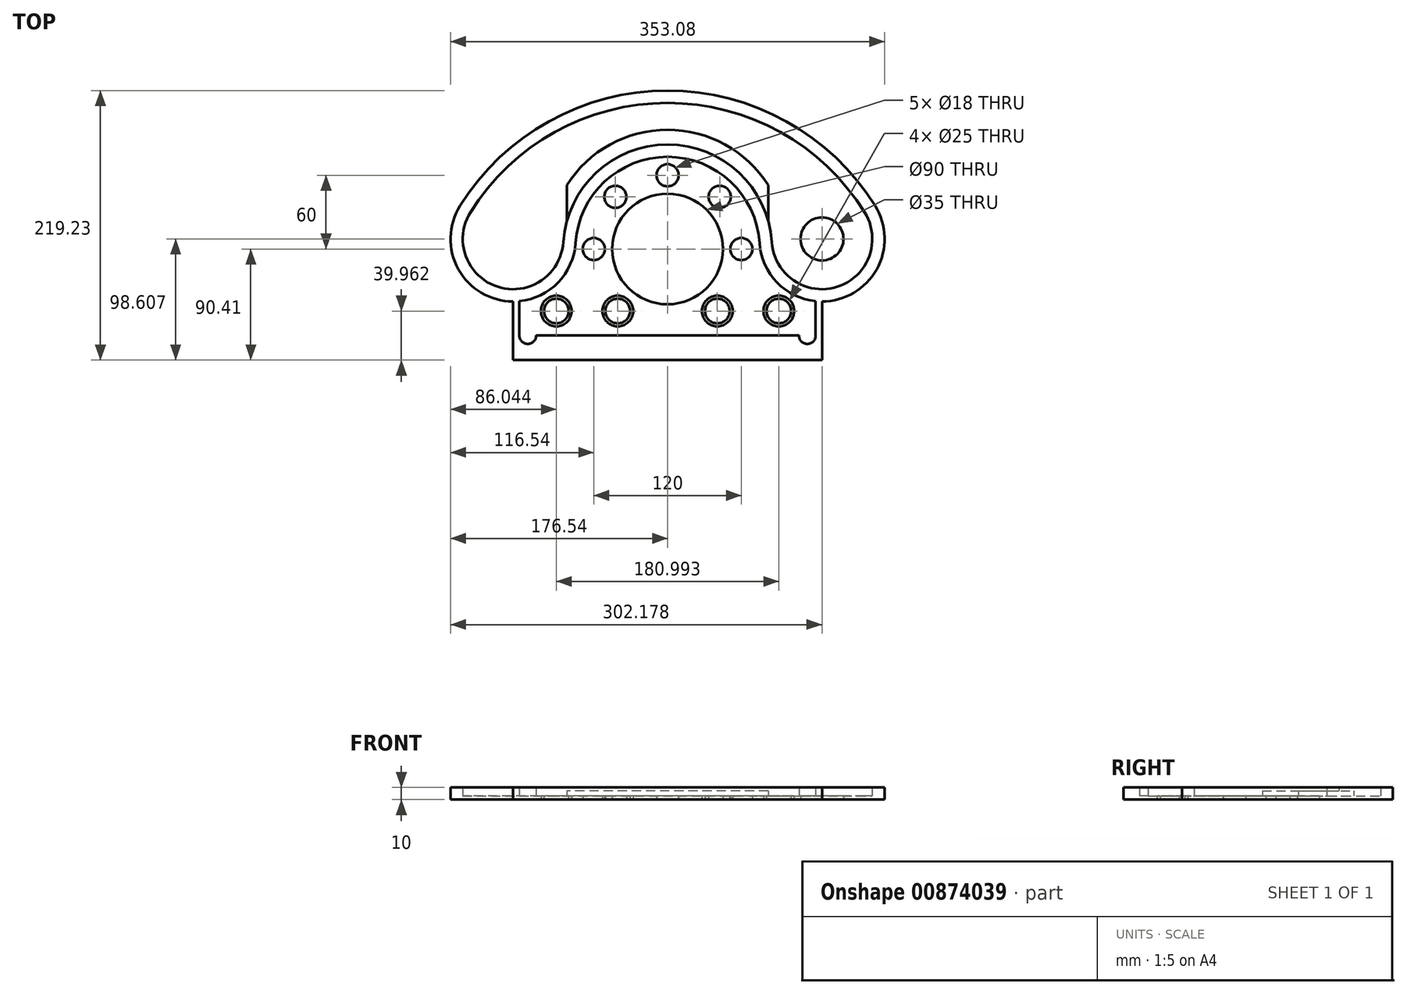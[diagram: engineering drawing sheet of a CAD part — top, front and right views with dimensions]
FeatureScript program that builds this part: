
annotation { "Feature Type Name" : "Feature", "Feature Type Description" : "" }
export const myFeature = defineFeature(function(context is Context, id is Id, definition is map)
    precondition{}
    {
        {
            var Q0;
            Q0=qCreatedBy(makeId("Top.planeOp"),FACE);
            var sketch = newSketch(context, id + "F0", { "sketchPlane" : qUnion([Q0])});
            skCircle(sketch, "E0", {"center": v(0, 0) * mm, "radius": 45 * mm});
            skArc(sketch, "E1", {"start": v(74.84, 4.88) * mm, "mid": v(0, 75) * mm, "end": v(-74.84, 4.88) * mm});
            skArc(sketch, "E2", {"start": v(84.82, 5.53) * mm, "mid": v(0, 85) * mm, "end": v(-84.82, 5.53) * mm});
            skLineSegment(sketch, "E3", {"start": v(-125.64, -32.7) * mm, "end": v(-125.64, -90.4) * mm});
            skLineSegment(sketch, "E4", {"start": v(-125.64, -90.4) * mm, "end": v(0, -90.4) * mm});
            skArc(sketch, "E5", {"start": v(-125.64, -32.7) * mm, "mid": v(-97.67, -21.65) * mm, "end": v(-84.82, 5.53) * mm});
            skArc(sketch, "E6", {"start": v(-120.5, -42.45) * mm, "mid": v(-89, -27.14) * mm, "end": v(-74.84, 4.88) * mm});
            skLineSegment(sketch, "E7", {"start": v(-120.5, -42.45) * mm, "end": v(-120.5, -70.4) * mm});
            skArc(sketch, "E8", {"start": v(-120.5, -70.4) * mm, "mid": v(-113.7, -77.21) * mm, "end": v(-106.9, -70.4) * mm});
            skLineSegment(sketch, "E9", {"start": v(-106.9, -70.4) * mm, "end": v(0, -70.4) * mm});
            skArc(sketch, "E10.MirrorCS", {"start": v(125.64, -32.7) * mm, "mid": v(97.67, -21.65) * mm, "end": v(84.82, 5.53) * mm});
            skArc(sketch, "E11.MirrorCS", {"start": v(120.5, -42.45) * mm, "mid": v(89, -27.14) * mm, "end": v(74.84, 4.88) * mm});
            skLineSegment(sketch, "E12.MirrorCS", {"start": v(125.64, -32.7) * mm, "end": v(125.64, -90.4) * mm});
            skLineSegment(sketch, "E13.MirrorCS", {"start": v(120.5, -42.45) * mm, "end": v(120.5, -70.4) * mm});
            skArc(sketch, "E14.MirrorCS", {"start": v(120.5, -70.4) * mm, "mid": v(113.7, -77.21) * mm, "end": v(106.9, -70.4) * mm});
            skLineSegment(sketch, "E15.MirrorCS", {"start": v(106.9, -70.4) * mm, "end": v(0, -70.4) * mm});
            skLineSegment(sketch, "E16.MirrorCS", {"start": v(125.64, -90.4) * mm, "end": v(0, -90.4) * mm});
            skPoint(sketch, "E17.orphan", {"position": v(125.64, -42.7) * mm});
            skPoint(sketch, "E18.orphan", {"position": v(-125.64, -42.7) * mm});
            skSolve(sketch);
        }
        {
            var Q0;
            {var subQ2=sQuery(id+"F0.wireOp",EDGE,"E1");Q0=makeQuery(id+"F0.imprint","IMPRINT",FACE,{"disambiguationData":[TD([[makeQuery(id+"F0.imprint","IMPRINT",EDGE,{"derivedFrom":subQ2}),-1.0]])]});}
            var Q1;
            Q1=makeQuery(id+"F0.imprint","IMPRINT",FACE,{"disambiguationData":[TD([[makeQuery(id+"F0.imprint","IMPRINT",EDGE,{"derivedFrom":sQuery(id+"F0.wireOp",EDGE,"E0")}),-1.0]])]});
            extrude(context, id + "F1", {"entities" : qUnion([Q0, Q1]), "depth" : 3 * mm, "offsetDistance" : 25 * mm});
        }
        {
            var Q0;
            Q0=qCreatedBy(makeId("Top.planeOp"),FACE);
            var sketch = newSketch(context, id + "F2", { "sketchPlane" : qUnion([Q0])});
            skPoint(sketch, "E19.0", {"position": v(125.64, 8.2) * mm});
            skPoint(sketch, "E20.0", {"position": v(125.64, -32.7) * mm});
            skArc(sketch, "E21", {"start": v(125.64, -32.7) * mm, "mid": v(161.4, -11.65) * mm, "end": v(160.35, 29.84) * mm});
            skArc(sketch, "E22", {"start": v(160.35, 29.84) * mm, "mid": v(91.69, 95.08) * mm, "end": v(0, 118.82) * mm});
            skArc(sketch, "E23.MirrorCS", {"start": v(-160.35, 29.84) * mm, "mid": v(-91.69, 95.08) * mm, "end": v(0, 118.82) * mm});
            skArc(sketch, "E24.MirrorC", {"start": v(-125.64, -32.7) * mm, "mid": v(-161.4, -11.65) * mm, "end": v(-160.35, 29.84) * mm});
            skArc(sketch, "E25.0", {"start": v(-125.64, -32.7) * mm, "mid": v(-97.67, -21.65) * mm, "end": v(-84.82, 5.53) * mm});
            skPoint(sketch, "E26.0", {"position": v(-81.93, 37.27) * mm});
            skArc(sketch, "E27.0", {"start": v(81.93, 51.92) * mm, "mid": v(0, 97) * mm, "end": v(-81.93, 51.92) * mm});
            skPoint(sketch, "E28.0", {"position": v(81.93, 37.27) * mm});
            skPoint(sketch, "E29.0", {"position": v(97.67, -21.65) * mm});
            skPoint(sketch, "E30.0", {"position": v(84.82, 5.53) * mm});
            skArc(sketch, "E31.0", {"start": v(125.64, -32.7) * mm, "mid": v(97.67, -21.65) * mm, "end": v(84.82, 5.53) * mm});
            skPoint(sketch, "E32.0", {"position": v(81.93, 22.63) * mm});
            skPoint(sketch, "E33.0", {"position": v(0, 85) * mm});
            skArc(sketch, "E34.0", {"start": v(84.82, 5.53) * mm, "mid": v(83.81, 14.15) * mm, "end": v(81.93, 22.63) * mm});
            skLineSegment(sketch, "E35.0", {"start": v(81.93, 22.63) * mm, "end": v(81.93, 51.92) * mm});
            skLineSegment(sketch, "E36.0", {"start": v(-81.93, 22.63) * mm, "end": v(-81.93, 51.92) * mm});
            skPoint(sketch, "E37.0", {"position": v(-81.93, 22.63) * mm});
            skPoint(sketch, "E38.0.end.orphan", {"position": v(-84.82, 5.53) * mm});
            skArc(sketch, "E39.0", {"start": v(-81.93, 22.63) * mm, "mid": v(-83.81, 14.15) * mm, "end": v(-84.82, 5.53) * mm});
            skSolve(sketch);
        }
        {
            var Q0;
            {var subQ2=sQuery(id+"F0.wireOp",EDGE,"E1");Q0=makeQuery(id+"F0.imprint","IMPRINT",FACE,{"disambiguationData":[TD([[makeQuery(id+"F0.imprint","IMPRINT",EDGE,{"derivedFrom":subQ2}),-1.0]])]});}
            extrude(context, id + "F3", {"entities" : qUnion([Q0]), "operationType" : NewBodyOperationType.ADD, "depth" : 10 * mm, "offsetDistance" : 25 * mm});
        }
        {
            var Q0;
            Q0=qCreatedBy(makeId("Top.planeOp"),FACE);
            var sketch = newSketch(context, id + "F4", { "sketchPlane" : qUnion([Q0])});
            skArc(sketch, "E40", {"start": v(81.93, 51.92) * mm, "mid": v(0, 97) * mm, "end": v(-81.93, 51.92) * mm});
            skLineSegment(sketch, "E41", {"start": v(-81.93, 22.63) * mm, "end": v(-81.93, 51.92) * mm});
            skArc(sketch, "E42.0", {"start": v(84.82, 5.53) * mm, "mid": v(0, 85) * mm, "end": v(-84.82, 5.53) * mm});
            skLineSegment(sketch, "E43.MirrorCS", {"start": v(81.93, 22.63) * mm, "end": v(81.93, 51.92) * mm});
            skPoint(sketch, "E44.orphan", {"position": v(-81.93, 0) * mm});
            skPoint(sketch, "E45.orphan", {"position": v(81.93, 0) * mm});
            skSolve(sketch);
        }
        {
            var Q0;
            Q0=makeQuery(id+"F4.imprint","IMPRINT",FACE,{"disambiguationData":[TD([[makeQuery(id+"F4.imprint","IMPRINT",EDGE,{"derivedFrom":sQuery(id+"F4.wireOp",EDGE,"E40")}),1.0]])]});
            extrude(context, id + "F5", {"entities" : qUnion([Q0]), "operationType" : NewBodyOperationType.ADD, "depth" : 7 * mm, "offsetDistance" : 25 * mm});
        }
        {
            var Q0;
            Q0=qSketchRegion(id+"F2",true);
            extrude(context, id + "F6", {"entities" : qUnion([Q0]), "operationType" : NewBodyOperationType.ADD, "depth" : 3 * mm, "offsetDistance" : 25 * mm});
        }
        {
            var Q0;
            Q0=makeQuery(id+"F0.imprint","IMPRINT",FACE,{"disambiguationData":[TD([[makeQuery(id+"F0.imprint","IMPRINT",EDGE,{"derivedFrom":sQuery(id+"F0.wireOp",EDGE,"E0")}),1.0]])]});
            var sketch = newSketch(context, id + "F7", { "sketchPlane" : qUnion([Q0])});
            skPoint(sketch, "E46.0", {"position": v(125.64, -90.4) * mm});
            skPoint(sketch, "E47.0", {"position": v(120.5, -42.45) * mm});
            skPoint(sketch, "E48.0", {"position": v(125.64, 8.2) * mm});
            skPoint(sketch, "E49.0", {"position": v(-120.5, -42.45) * mm});
            skPoint(sketch, "E50.0", {"position": v(-125.64, 8.2) * mm});
            skPoint(sketch, "E51.0", {"position": v(-125.64, -90.4) * mm});
            skPoint(sketch, "E52.0", {"position": v(0, -70.15) * mm});
            skArc(sketch, "E53", {"start": v(125.64, -42.7) * mm, "mid": v(170.15, -16.5) * mm, "end": v(168.83, 35.13) * mm});
            skArc(sketch, "E54", {"start": v(-168.83, 35.13) * mm, "mid": v(-170.15, -16.5) * mm, "end": v(-125.64, -42.7) * mm});
            skArc(sketch, "E55", {"start": v(168.83, 35.13) * mm, "mid": v(0, 128.82) * mm, "end": v(-168.83, 35.13) * mm});
            skPoint(sketch, "E56.0", {"position": v(-125.64, -32.7) * mm});
            skPoint(sketch, "E57.0", {"position": v(-125.64, -42.7) * mm});
            skPoint(sketch, "E58.0", {"position": v(125.64, -32.7) * mm});
            skPoint(sketch, "E59.0", {"position": v(125.64, -42.7) * mm});
            skLineSegment(sketch, "E60", {"start": v(125.64, -42.7) * mm, "end": v(125.64, -32.7) * mm});
            skLineSegment(sketch, "E61", {"start": v(-125.64, -42.7) * mm, "end": v(-125.64, -32.7) * mm});
            skArc(sketch, "E62.2", {"start": v(125.64, -32.7) * mm, "mid": v(161.4, -11.65) * mm, "end": v(160.35, 29.84) * mm});
            skArc(sketch, "E62.3", {"start": v(160.35, 29.84) * mm, "mid": v(91.69, 95.08) * mm, "end": v(0, 118.82) * mm});
            skArc(sketch, "E62.4", {"start": v(-160.35, 29.84) * mm, "mid": v(-91.69, 95.08) * mm, "end": v(0, 118.82) * mm});
            skArc(sketch, "E62.5", {"start": v(-125.64, -32.7) * mm, "mid": v(-161.4, -11.65) * mm, "end": v(-160.35, 29.84) * mm});
            skPoint(sketch, "E62.9", {"position": v(-161.4, -11.65) * mm});
            skSolve(sketch);
        }
        {
            var Q0;
            Q0=makeQuery(id+"F7.imprint","IMPRINT",FACE,{"disambiguationData":[TD([[makeQuery(id+"F7.imprint","IMPRINT",EDGE,{"derivedFrom":sQuery(id+"F7.wireOp",EDGE,"E53")}),1.0]])]});
            extrude(context, id + "F8", {"entities" : qUnion([Q0]), "operationType" : NewBodyOperationType.ADD, "depth" : 10 * mm, "offsetDistance" : 25 * mm});
        }
        {
            var Q0;
            Q0=makeQuery(id+"F0.imprint","IMPRINT",FACE,{"disambiguationData":[TD([[makeQuery(id+"F0.imprint","IMPRINT",EDGE,{"derivedFrom":sQuery(id+"F0.wireOp",EDGE,"E0")}),1.0]])]});
            var sketch = newSketch(context, id + "F9", { "sketchPlane" : qUnion([Q0])});
            skPoint(sketch, "E63.0", {"position": v(125.64, 8.2) * mm});
            skPoint(sketch, "E64.0", {"position": v(-125.64, 8.2) * mm});
            skCircle(sketch, "E65", {"center": v(125.64, 8.2) * mm, "radius": 17.5 * mm});
            skPoint(sketch, "E66.0", {"position": v(120.5, -56.43) * mm});
            skPoint(sketch, "E67.0", {"position": v(-120.5, -56.43) * mm});
            skPoint(sketch, "E68.0", {"position": v(-120.5, -42.45) * mm});
            skPoint(sketch, "E69.0", {"position": v(120.5, -42.45) * mm});
            skLineSegment(sketch, "E70", {"start": v(-120.5, -42.45) * mm, "end": v(-120.5, -50.45) * mm});
            skLineSegment(sketch, "E71", {"start": v(-120.5, -50.45) * mm, "end": v(120.5, -50.45) * mm});
            skLineSegment(sketch, "E72", {"start": v(-120.5, -50.45) * mm, "end": v(-90.5, -50.45) * mm});
            skLineSegment(sketch, "E73", {"start": v(-90.5, -50.45) * mm, "end": v(9.5, -50.45) * mm});
            skLineSegment(sketch, "E74", {"start": v(-90.5, -50.45) * mm, "end": v(-40.5, -50.45) * mm});
            skLineSegment(sketch, "E75", {"start": v(120.5, -50.45) * mm, "end": v(90.5, -50.45) * mm});
            skLineSegment(sketch, "E76", {"start": v(90.5, -50.45) * mm, "end": v(40.5, -50.45) * mm});
            skCircle(sketch, "E77", {"center": v(-90.5, -50.45) * mm, "radius": 12.5 * mm});
            skCircle(sketch, "E78", {"center": v(-40.5, -50.45) * mm, "radius": 12.5 * mm});
            skCircle(sketch, "E79", {"center": v(40.5, -50.45) * mm, "radius": 12.5 * mm});
            skCircle(sketch, "E80", {"center": v(90.5, -50.45) * mm, "radius": 12.5 * mm});
            skCircle(sketch, "E81", {"center": v(-90.5, -50.45) * mm, "radius": 10 * mm});
            skCircle(sketch, "E82", {"center": v(-40.5, -50.45) * mm, "radius": 10 * mm});
            skCircle(sketch, "E83", {"center": v(40.5, -50.45) * mm, "radius": 10 * mm});
            skCircle(sketch, "E84", {"center": v(90.5, -50.45) * mm, "radius": 10 * mm});
            skSolve(sketch);
        }
        {
            var Q0;
            Q0=makeQuery(id+"F9.imprint","IMPRINT",FACE,{"disambiguationData":[TD([[makeQuery(id+"F9.imprint","IMPRINT",EDGE,{"derivedFrom":sQuery(id+"F9.wireOp",EDGE,"E65")}),1.0]])]});
            extrude(context, id + "F10", {"entities" : qUnion([Q0]), "operationType" : NewBodyOperationType.REMOVE, "depth" : 25 * mm, "offsetDistance" : 25 * mm});
        }
        {
            var Q0;
            Q0=makeQuery(id+"F0.imprint","IMPRINT",FACE,{"disambiguationData":[TD([[makeQuery(id+"F0.imprint","IMPRINT",EDGE,{"derivedFrom":sQuery(id+"F0.wireOp",EDGE,"E0")}),1.0]])]});
            var sketch = newSketch(context, id + "F11", { "sketchPlane" : qUnion([Q0])});
            skCircle(sketch, "E85.0", {"center": v(0, 0) * mm, "radius": 45 * mm});
            skLineSegment(sketch, "E86.0.0", {"start": v(-106.9, -70.4) * mm, "end": v(106.9, -70.4) * mm});
            skArc(sketch, "E86.0.1", {"start": v(106.9, -70.4) * mm, "mid": v(113.7, -77.21) * mm, "end": v(120.5, -70.4) * mm});
            skLineSegment(sketch, "E86.0.2", {"start": v(120.5, -70.4) * mm, "end": v(120.5, -42.45) * mm});
            skArc(sketch, "E86.0.3", {"start": v(120.5, -42.45) * mm, "mid": v(89, -27.14) * mm, "end": v(74.84, 4.88) * mm});
            skArc(sketch, "E86.0.4", {"start": v(-74.84, 4.88) * mm, "mid": v(0, 75) * mm, "end": v(74.84, 4.88) * mm});
            skArc(sketch, "E86.0.5", {"start": v(-74.84, 4.88) * mm, "mid": v(-89, -27.14) * mm, "end": v(-120.5, -42.45) * mm});
            skLineSegment(sketch, "E86.0.6", {"start": v(-120.5, -42.45) * mm, "end": v(-120.5, -70.4) * mm});
            skArc(sketch, "E86.0.7", {"start": v(-106.9, -70.4) * mm, "mid": v(-113.7, -77.21) * mm, "end": v(-120.5, -70.4) * mm});
            skLineSegment(sketch, "E87", {"start": v(0, 0) * mm, "end": v(0, 45) * mm});
            skLineSegment(sketch, "E88", {"start": v(0, 45) * mm, "end": v(0, 60) * mm});
            skLineSegment(sketch, "E89", {"start": v(0, 0) * mm, "end": v(45, 0) * mm});
            skLineSegment(sketch, "E90", {"start": v(0, 0) * mm, "end": v(-45, 0) * mm});
            skLineSegment(sketch, "E91", {"start": v(-45, 0) * mm, "end": v(-60, 0) * mm});
            skLineSegment(sketch, "E92", {"start": v(45, 0) * mm, "end": v(60, 0) * mm});
            skCircle(sketch, "E93", {"center": v(0, 60) * mm, "radius": 9 * mm});
            skCircle(sketch, "E94", {"center": v(60, 0) * mm, "radius": 9 * mm});
            skCircle(sketch, "E95", {"center": v(-60, 0) * mm, "radius": 9 * mm});
            skCircle(sketch, "E96", {"center": v(42.43, 42.43) * mm, "radius": 9 * mm});
            skCircle(sketch, "E97", {"center": v(-42.43, 42.43) * mm, "radius": 9 * mm});
            skSolve(sketch);
        }
        {
            var Q0;
            Q0=makeQuery(id+"F11.imprint","IMPRINT",FACE,{"disambiguationData":[TD([[makeQuery(id+"F11.imprint","IMPRINT",EDGE,{"derivedFrom":sQuery(id+"F11.wireOp",EDGE,"E95")}),1.0]])]});
            var Q1;
            Q1=makeQuery(id+"F11.imprint","IMPRINT",FACE,{"disambiguationData":[TD([[makeQuery(id+"F11.imprint","IMPRINT",EDGE,{"derivedFrom":sQuery(id+"F11.wireOp",EDGE,"E97")}),1.0]])]});
            var Q2;
            Q2=makeQuery(id+"F11.imprint","IMPRINT",FACE,{"disambiguationData":[TD([[makeQuery(id+"F11.imprint","IMPRINT",EDGE,{"derivedFrom":sQuery(id+"F11.wireOp",EDGE,"E93")}),1.0]])]});
            var Q3;
            Q3=makeQuery(id+"F11.imprint","IMPRINT",FACE,{"disambiguationData":[TD([[makeQuery(id+"F11.imprint","IMPRINT",EDGE,{"derivedFrom":sQuery(id+"F11.wireOp",EDGE,"E96")}),1.0]])]});
            var Q4;
            Q4=makeQuery(id+"F11.imprint","IMPRINT",FACE,{"disambiguationData":[TD([[makeQuery(id+"F11.imprint","IMPRINT",EDGE,{"derivedFrom":sQuery(id+"F11.wireOp",EDGE,"E94")}),1.0]])]});
            var Q5;
            Q5=sQuery(id+"F11.wireOp",EDGE,"E97");
            var Q6;
            Q6=sQuery(id+"F11.wireOp",EDGE,"E93");
            var Q7;
            Q7=sQuery(id+"F11.wireOp",EDGE,"E96");
            var Q8;
            Q8=sQuery(id+"F11.wireOp",EDGE,"E94");
            var Q9;
            Q9=sQuery(id+"F11.wireOp",EDGE,"E95");
            extrude(context, id + "F12", {"entities" : qUnion([Q0, Q1, Q2, Q3, Q4]), "operationType" : NewBodyOperationType.REMOVE, "surfaceEntities" : qUnion([Q5, Q6, Q7, Q8, Q9]), "depth" : 25 * mm, "offsetDistance" : 25 * mm});
        }
        {
            var Q0;
            {var subQ0=sQuery(id+"F9.wireOp",EDGE,"E76");var subQ1=sQuery(id+"F9.wireOp",EDGE,"E75");var subQ2=makeQuery(id+"F9.imprint","INTERSECT",VERTEX,{"derivedFrom":[subQ1,subQ0]});Q0=makeQuery(id+"F9.imprint","IMPRINT",FACE,{"disambiguationData":[TD([[makeQuery(id+"F9.imprint","IMPRINT",EDGE,{"disambiguationData":[TD([[subQ2,1.0]])],"derivedFrom":subQ1}),1.0]])]});}
            var Q1;
            {var subQ0=sQuery(id+"F9.wireOp",EDGE,"E76");var subQ1=sQuery(id+"F9.wireOp",EDGE,"E75");var subQ2=makeQuery(id+"F9.imprint","INTERSECT",VERTEX,{"derivedFrom":[subQ1,subQ0]});Q1=makeQuery(id+"F9.imprint","IMPRINT",FACE,{"disambiguationData":[TD([[makeQuery(id+"F9.imprint","IMPRINT",EDGE,{"disambiguationData":[TD([[subQ2,1.0]])],"derivedFrom":subQ1}),-1.0]])]});}
            var Q2;
            {var subQ0=sQuery(id+"F9.wireOp",EDGE,"E76");var subQ1=sQuery(id+"F9.wireOp",EDGE,"E71");var subQ2=makeQuery(id+"F9.imprint","INTERSECT",VERTEX,{"derivedFrom":[subQ1,subQ0]});Q2=makeQuery(id+"F9.imprint","IMPRINT",FACE,{"disambiguationData":[TD([[makeQuery(id+"F9.imprint","IMPRINT",EDGE,{"disambiguationData":[TD([[subQ2,1.0]])],"derivedFrom":subQ1}),1.0]])]});}
            var Q3;
            {var subQ0=sQuery(id+"F9.wireOp",EDGE,"E76");var subQ1=sQuery(id+"F9.wireOp",EDGE,"E71");var subQ2=makeQuery(id+"F9.imprint","INTERSECT",VERTEX,{"derivedFrom":[subQ1,subQ0]});Q3=makeQuery(id+"F9.imprint","IMPRINT",FACE,{"disambiguationData":[TD([[makeQuery(id+"F9.imprint","IMPRINT",EDGE,{"disambiguationData":[TD([[subQ2,1.0]])],"derivedFrom":subQ1}),-1.0]])]});}
            var Q4;
            {var subQ0=sQuery(id+"F9.wireOp",EDGE,"E74");var subQ1=sQuery(id+"F9.wireOp",EDGE,"E73");var subQ2=makeQuery(id+"F9.imprint","INTERSECT",VERTEX,{"derivedFrom":[subQ1,subQ0]});Q4=makeQuery(id+"F9.imprint","IMPRINT",FACE,{"disambiguationData":[TD([[makeQuery(id+"F9.imprint","IMPRINT",EDGE,{"disambiguationData":[TD([[subQ2,-1.0]])],"derivedFrom":subQ1}),1.0]])]});}
            var Q5;
            {var subQ0=sQuery(id+"F9.wireOp",EDGE,"E74");var subQ1=sQuery(id+"F9.wireOp",EDGE,"E73");var subQ2=makeQuery(id+"F9.imprint","INTERSECT",VERTEX,{"derivedFrom":[subQ1,subQ0]});Q5=makeQuery(id+"F9.imprint","IMPRINT",FACE,{"disambiguationData":[TD([[makeQuery(id+"F9.imprint","IMPRINT",EDGE,{"disambiguationData":[TD([[subQ2,-1.0]])],"derivedFrom":subQ1}),-1.0]])]});}
            var Q6;
            {var subQ0=sQuery(id+"F9.wireOp",EDGE,"E74");var subQ1=sQuery(id+"F9.wireOp",EDGE,"E72");var subQ2=makeQuery(id+"F9.imprint","INTERSECT",VERTEX,{"derivedFrom":[subQ1,subQ0]});Q6=makeQuery(id+"F9.imprint","IMPRINT",FACE,{"disambiguationData":[TD([[makeQuery(id+"F9.imprint","IMPRINT",EDGE,{"disambiguationData":[TD([[subQ2,1.0]])],"derivedFrom":subQ1}),1.0]])]});}
            var Q7;
            {var subQ0=sQuery(id+"F9.wireOp",EDGE,"E74");var subQ1=sQuery(id+"F9.wireOp",EDGE,"E72");var subQ2=makeQuery(id+"F9.imprint","INTERSECT",VERTEX,{"derivedFrom":[subQ1,subQ0]});Q7=makeQuery(id+"F9.imprint","IMPRINT",FACE,{"disambiguationData":[TD([[makeQuery(id+"F9.imprint","IMPRINT",EDGE,{"disambiguationData":[TD([[subQ2,1.0]])],"derivedFrom":subQ1}),-1.0]])]});}
            var Q8;
            Q8=sQuery(id+"F9.wireOp",EDGE,"E84");
            var Q9;
            Q9=sQuery(id+"F9.wireOp",EDGE,"E83");
            var Q10;
            Q10=sQuery(id+"F9.wireOp",EDGE,"E82");
            var Q11;
            Q11=sQuery(id+"F9.wireOp",EDGE,"E81");
            extrude(context, id + "F13", {"entities" : qUnion([Q0, Q1, Q2, Q3, Q4, Q5, Q6, Q7]), "operationType" : NewBodyOperationType.REMOVE, "surfaceEntities" : qUnion([Q8, Q9, Q10, Q11]), "depth" : 25 * mm, "offsetDistance" : 25 * mm});
        }
    });
